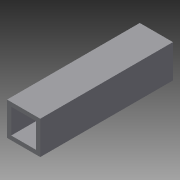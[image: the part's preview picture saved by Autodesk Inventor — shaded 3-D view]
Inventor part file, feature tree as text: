
AUTODESK INVENTOR PART (.ipt)
format: ipt  version: 2013 (Build 170138000, 138)  size: 71,680 bytes
history: native  units: in
note: dims shown in document units (in); Inventor stores cm internally (conversion verified against a paired STEP export)
features: extrude x1, sketch x1
ambient origin geometry x8: Origin, YZ Plane, XZ Plane, XY Plane, X Axis, Y Axis, Z Axis, Center Point
bodies: Solid1 (feature_tree)
feature tree (2):
  extrude  "Extrusion1"  Depth=1.0in
  sketch  "Sketch1"  dims[d0=1.0in d2=1.0in d3=0.125in d4=4.0in d5=0.0in]
